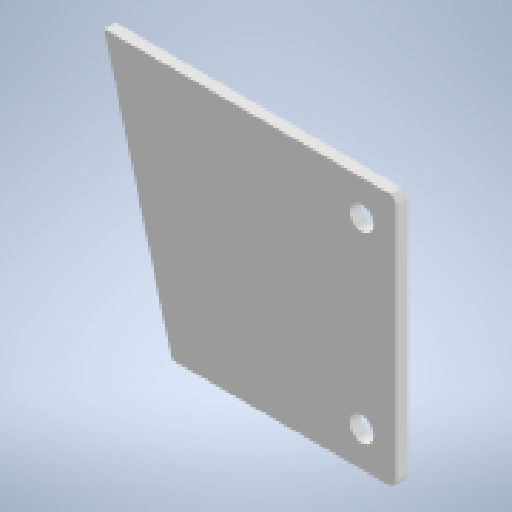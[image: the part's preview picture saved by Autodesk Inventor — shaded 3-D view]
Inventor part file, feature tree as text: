
AUTODESK INVENTOR PART (.ipt)
format: ipt  version: 2024.2 (Build 282272000, 272)  size: 148,480 bytes
history: native  units: mm
features: sketch x2, sheet_metal_op x1, hole x1, chamfer x1, other x1
ambient origin geometry x8: Origin, YZ Plane, XZ Plane, XY Plane, X Axis, Y Axis, Z Axis, Center Point
bodies: Solid1 (feature_tree)
feature tree (6):
  sheet_metal_op  "Face1"
  hole  "Hole1"  [1 undecoded]
  chamfer  "Corner Round1"
  sketch  "Sketch1"  dims[d0=170.0mm d1=180.0mm]
  other  "Plate1"
  sketch  "Sketch2"  dims[d2=8.0mm d3=17.0mm d4=6.0mm d5=4.0mm d6=2.0mm d7=90.0deg d8=8.0mm d9=20.594885mm d10=25.0mm d12=25.0mm d13=6.0mm d14=15.0deg]
note: 1 required parameter value undecoded (feature->parameter linkage not recoverable at this tier; creation-order binding heuristic only, values carry confidence <= 0.55)
